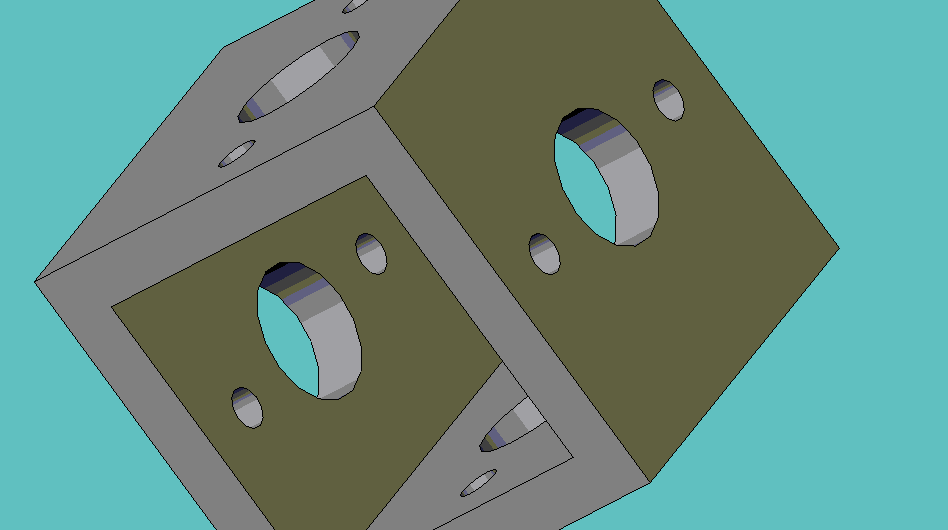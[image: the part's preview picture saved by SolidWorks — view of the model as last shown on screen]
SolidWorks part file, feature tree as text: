
SOLIDWORKS PART (.sldprt)
format: sldprt  version: not decoded by parser v0  size: 115,712 bytes
history: native  units: mm
features: sketch x3, cut_extrude x2, material x1, extrude x1 (+12 scaffold rows collapsed)
feature tree (19):
  scaffold x12  (default folders/planes/origin — collapsed)
  material  "Material <not specified>"
  sketch  "Sketch1"  dims[D1=3.175mm]
  extrude  "Extrude1"  Depth=25.4mm
  sketch  "Sketch2"  dims[D1=14.6812mm]
  sketch  "Sketch3"
  cut_extrude  "Cut-Extrude1"  Depth=25.4mm
  cut_extrude  "Cut-Extrude2"  Depth=25.4mm
decode coverage: 5 of 6 modeling features carry decoded parameters
note: suppression state not decoded; provenance and decode notes live in map.json
